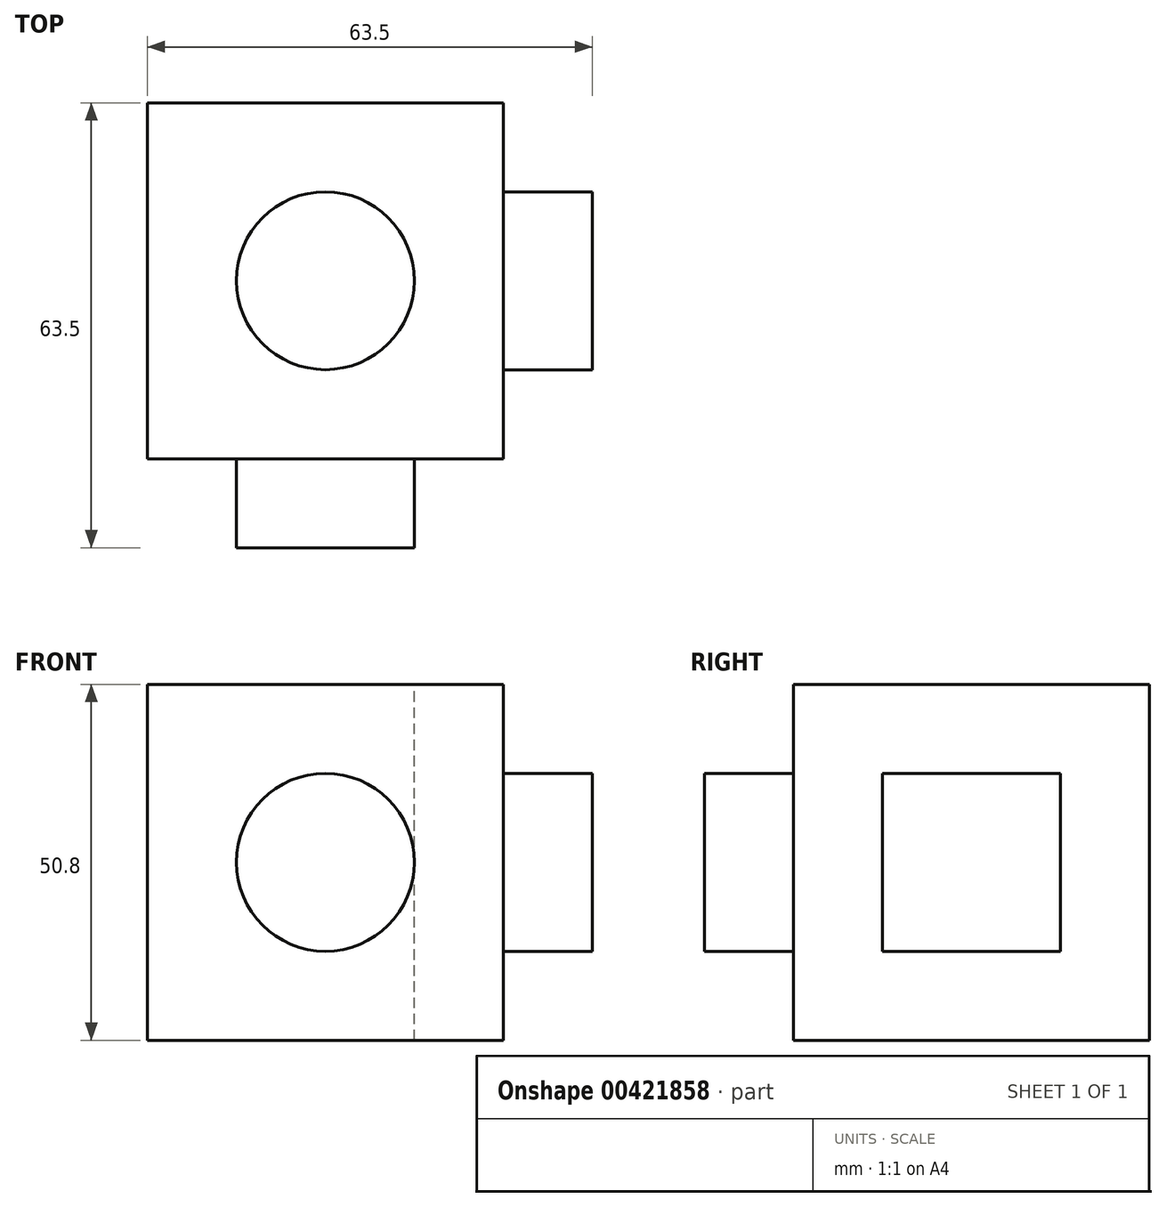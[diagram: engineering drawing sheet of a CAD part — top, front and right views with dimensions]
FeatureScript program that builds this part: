
annotation { "Feature Type Name" : "Feature", "Feature Type Description" : "" }
export const myFeature = defineFeature(function(context is Context, id is Id, definition is map)
    precondition{}
    {
        {
            var Q0;
            Q0=qCreatedBy(makeId("Front.planeOp"),FACE);
            var sketch = newSketch(context, id + "F0", { "sketchPlane" : qUnion([Q0])});
            skLineSegment(sketch, "E0.bottom", {"start": v(0, 0) * mm, "end": v(-50.8, 0) * mm});
            skLineSegment(sketch, "E0.top", {"start": v(0, 50.8) * mm, "end": v(-50.8, 50.8) * mm});
            skLineSegment(sketch, "E0.left", {"start": v(0, 0) * mm, "end": v(0, 50.8) * mm});
            skLineSegment(sketch, "E0.right", {"start": v(-50.8, 0) * mm, "end": v(-50.8, 50.8) * mm});
            skSolve(sketch);
        }
        {
            var Q0;
            Q0 = qSketchRegion(id + "F0", true);
            extrude(context, id + "F1", {"entities" : qUnion([Q0]), "depth" : 50.8 * mm});
        }
        {
            var Q0;
            Q0=makeQuery(id+"F1.opExtrude","SWEPT_FACE",FACE,{"disambiguationData":[OSD([sQuery(id+"F0.wireOp",EDGE,"E0.top")])]});
            var sketch = newSketch(context, id + "F2", { "sketchPlane" : qUnion([Q0])});
            skCircle(sketch, "E1", {"center": v(-25.4, -25.4) * mm, "radius": 12.7 * mm});
            skSolve(sketch);
        }
        {
            var Q0;
            Q0=makeQuery(id+"F2.imprint","IMPRINT",FACE,{"disambiguationData":[TD([[makeQuery(id+"F2.imprint","IMPRINT",EDGE,{"derivedFrom":sQuery(id+"F2.wireOp",EDGE,"E1")}),1.0]])]});
            extrude(context, id + "F3", {"entities" : qUnion([Q0]), "operationType" : NewBodyOperationType.ADD, "depth" : 50.8 * mm});
        }
        {
            var Q0;
            Q0=makeQuery(id+"F3.opExtrude","CAP_FACE",FACE,{"disambiguationData":[OSD([sQuery(id+"F2.wireOp",EDGE,"E1")])],"isStart":false});
            extrude(context, id + "F4", {"entities" : qUnion([Q0]), "operationType" : NewBodyOperationType.REMOVE, "oppositeDirection" : true, "depth" : 101.6 * mm});
        }
        {
            var Q0;
            Q0=makeQuery(id+"F1.opExtrude","CAP_FACE",FACE,{"disambiguationData":[OSD([sQuery(id+"F0.wireOp",EDGE,"E0.bottom"),sQuery(id+"F0.wireOp",EDGE,"E0.top"),sQuery(id+"F0.wireOp",EDGE,"E0.left"),sQuery(id+"F0.wireOp",EDGE,"E0.right")])],"isStart":false});
            var sketch = newSketch(context, id + "F5", { "sketchPlane" : qUnion([Q0])});
            skCircle(sketch, "E2", {"center": v(-25.4, 25.4) * mm, "radius": 12.7 * mm});
            skSolve(sketch);
        }
        {
            var Q0;
            Q0 = qSketchRegion(id + "F5", true);
            extrude(context, id + "F6", {"entities" : qUnion([Q0]), "operationType" : NewBodyOperationType.ADD, "depth" : 12.7 * mm});
        }
        {
            var Q0;
            Q0=makeQuery(id+"F1.opExtrude","SWEPT_FACE",FACE,{"disambiguationData":[OSD([sQuery(id+"F0.wireOp",EDGE,"E0.left")])]});
            var sketch = newSketch(context, id + "F7", { "sketchPlane" : qUnion([Q0])});
            skLineSegment(sketch, "E3.bottom", {"start": v(-38.1, 38.1) * mm, "end": v(-12.7, 38.1) * mm});
            skLineSegment(sketch, "E3.top", {"start": v(-38.1, 12.7) * mm, "end": v(-12.7, 12.7) * mm});
            skLineSegment(sketch, "E3.left", {"start": v(-38.1, 38.1) * mm, "end": v(-38.1, 12.7) * mm});
            skLineSegment(sketch, "E3.right", {"start": v(-12.7, 38.1) * mm, "end": v(-12.7, 12.7) * mm});
            skSolve(sketch);
        }
        {
            var Q0;
            Q0=makeQuery(id+"F7.imprint","IMPRINT",FACE,{"disambiguationData":[TD([[makeQuery(id+"F7.imprint","IMPRINT",EDGE,{"derivedFrom":sQuery(id+"F7.wireOp",EDGE,"E3.bottom")}),-1.0]])]});
            extrude(context, id + "F8", {"entities" : qUnion([Q0]), "operationType" : NewBodyOperationType.ADD, "depth" : 12.7 * mm});
        }
    });
